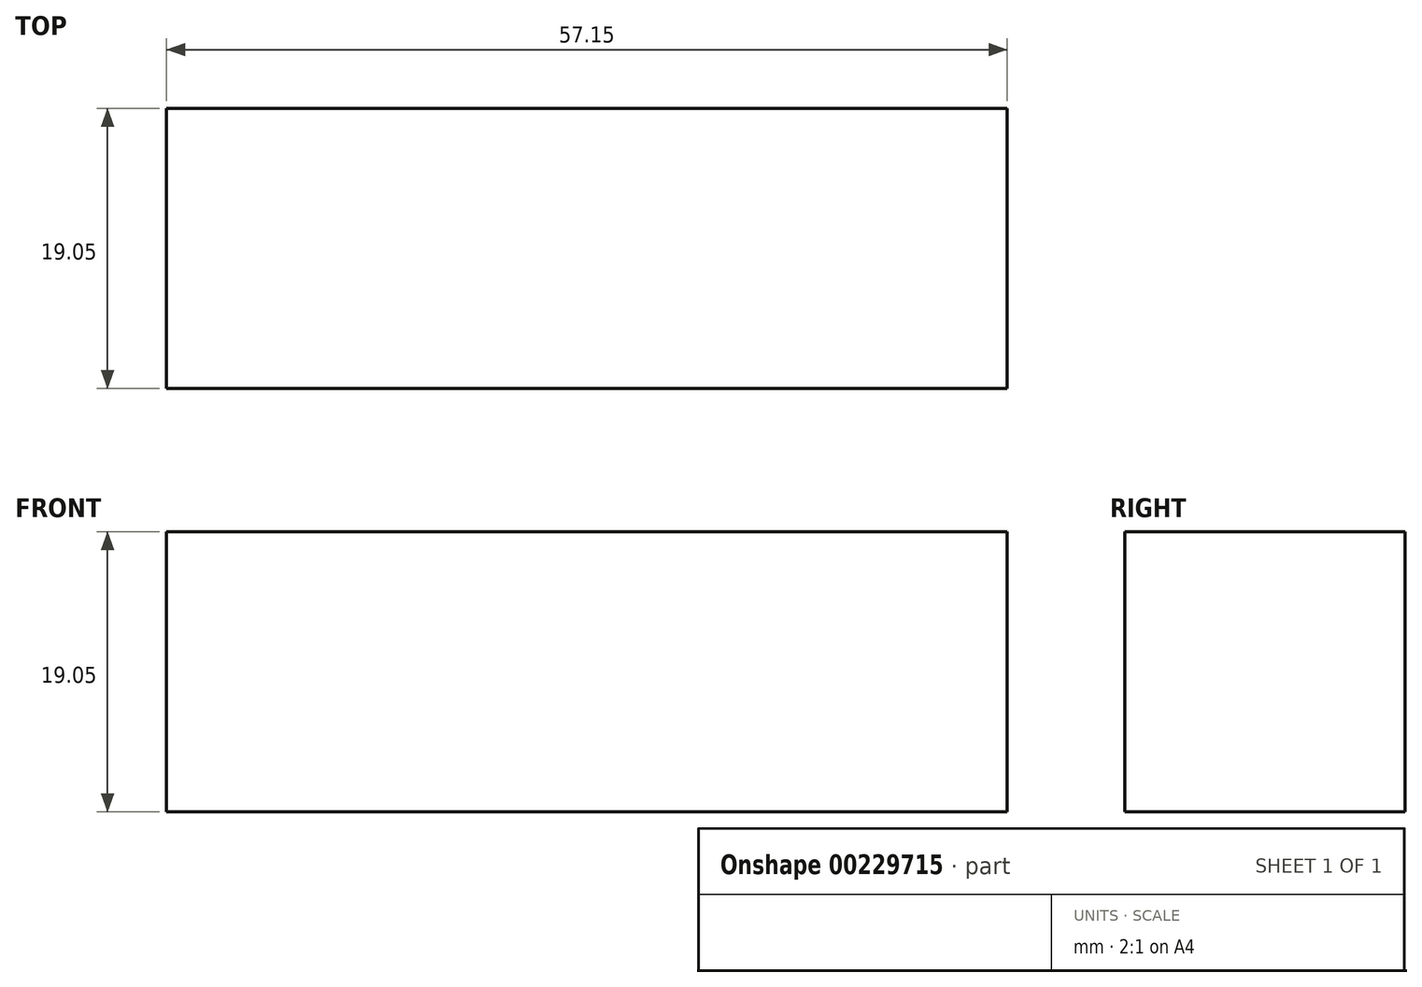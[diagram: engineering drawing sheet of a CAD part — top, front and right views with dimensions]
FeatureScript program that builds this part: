
annotation { "Feature Type Name" : "Feature", "Feature Type Description" : "" }
export const myFeature = defineFeature(function(context is Context, id is Id, definition is map)
    precondition{}
    {
        {
            var Q0;
            Q0=qCreatedBy(makeId("Front.planeOp"),FACE);
            var sketch = newSketch(context, id + "F0", { "sketchPlane" : qUnion([Q0])});
            skLineSegment(sketch, "E0.bottom", {"start": v(-42.82, 12.8) * mm, "end": v(14.33, 12.8) * mm});
            skLineSegment(sketch, "E0.top", {"start": v(-42.82, -6.25) * mm, "end": v(14.33, -6.25) * mm});
            skLineSegment(sketch, "E0.left", {"start": v(-42.82, 12.8) * mm, "end": v(-42.82, -6.25) * mm});
            skLineSegment(sketch, "E0.right", {"start": v(14.33, 12.8) * mm, "end": v(14.33, -6.25) * mm});
            skSolve(sketch);
        }
        {
            var Q0;
            Q0 = qSketchRegion(id + "F0", true);
            extrude(context, id + "F1", {"entities" : qUnion([Q0]), "depth" : 19.05 * mm});
        }
    });
